# Revit family: Haworth_Maari_Chair_LegBase
name_source: partatom
category: Furniture
revit_build: Autodesk Revit 2018 (Build: 20170223_1515(x64)
units: mm (PartAtom-declared; Revit-internal decimal feet)

## family parameters
Always vertical = Yes
Cut with Voids When Loaded = No
OmniClass Number = 23.40.70.14.64.21
OmniClass Title = Systems Furniture
Room Calculation Point = No
Shared = No
Work Plane-Based = No

## types (5) — shared parameters
Arm Cap Finish = Haworth _ Polymer _ Water TR-1W
Assembly Code = E2020200
Glide or Caster Option = Option only available for Four-Leg Chair
Manufacturer = Haworth
Model = Haworth Maari
Revision Number = 2
Size = Verify Final Dim. w/ Haworth
Sustainability Info = https://www.haworth.com
URL = www.haworth.com
URL - Product = https://www.haworth.com
Warranty = http://www.haworth.com

## per-type parameters (varying)
| type | Actual Depth | Actual Height | Actual Width | Casters | Description | Four Leg Arm Control | Four Legs | Glides | Sled Base | Sled Leg Arm Control | With Arms | Wood Base |
| S7W - Wood Legs - No Arms | 21 1/2" | 34" | 19 1/2" | No | Haworth Maari Chair - Wood Leg - No Arms | No | No | Yes | No | No | No | Yes |
| S7H - Sled Base - With Arms | 21 3/4" | 33 3/4" | 22" | No | Haworth Maari Chair - Sled Base - With Arms | No | No | Yes | Yes | Yes | Yes | No |
| S7S - Four Leg - With Arms | 21 1/2" | 33" | 23" | Yes | Haworth Maari Chair - Four Leg - With Arms | Yes | Yes | No | No | No | Yes | No |
| S7S - Four Leg - No Arms | 21 1/2" | 33" | 23" | Yes | Haworth Maari Chair - Four Leg - No Arms | No | Yes | No | No | No | No | No |
| S7H - Sled Base - No Arms | 21 3/4" | 33 3/4" | 22" | No | Haworth Maari Chair - Sled Base - No Arms | No | No | Yes | Yes | No | No | No |

## geometry (parser evidence)
native form markers: Sweep x8
no freeform markers — native parametric forms only
